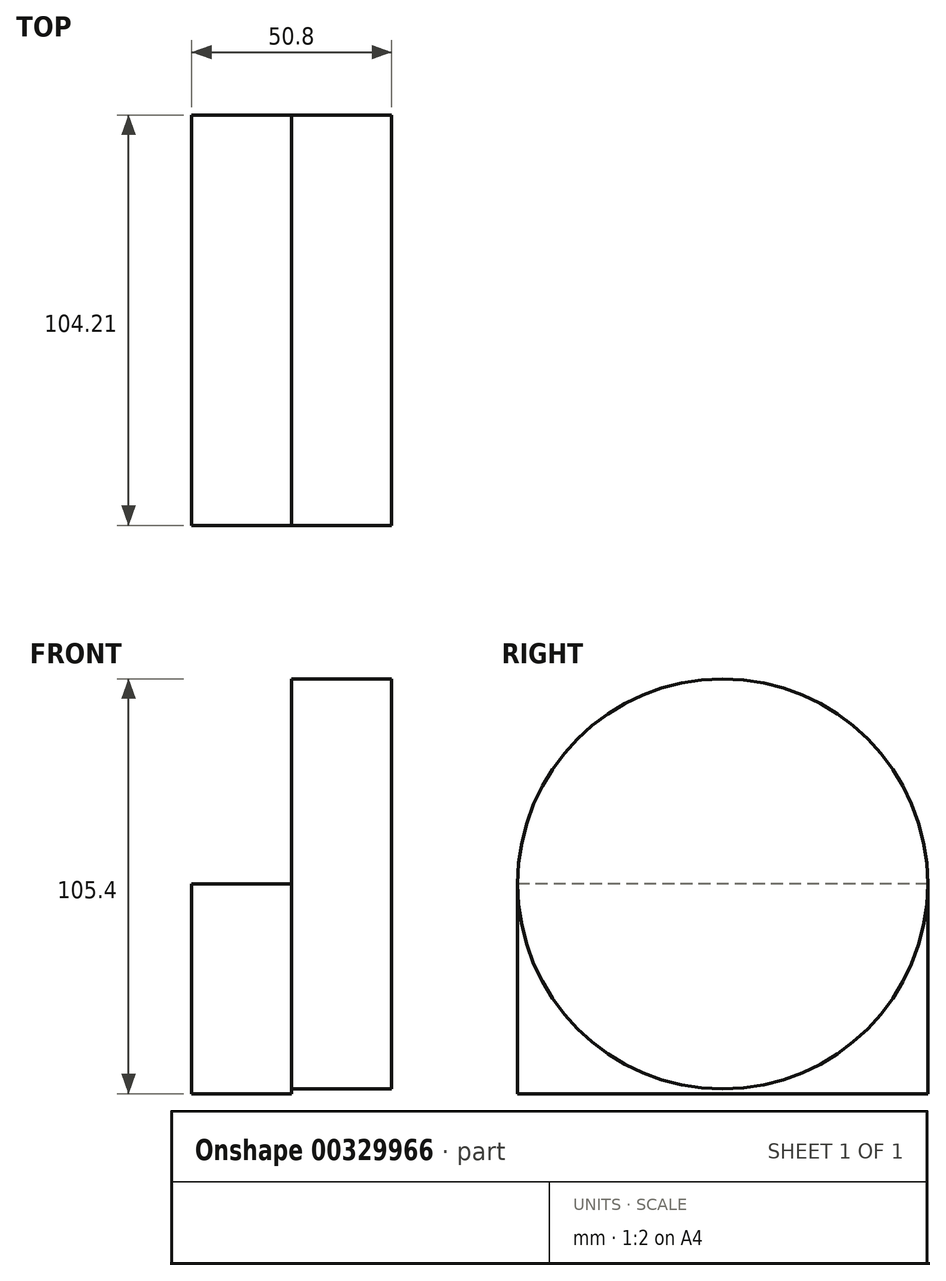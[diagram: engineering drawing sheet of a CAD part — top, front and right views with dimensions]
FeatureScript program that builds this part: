
annotation { "Feature Type Name" : "Feature", "Feature Type Description" : "" }
export const myFeature = defineFeature(function(context is Context, id is Id, definition is map)
    precondition{}
    {
        {
            var Q0;
            Q0=qCreatedBy(makeId("Right.planeOp"),FACE);
            var sketch = newSketch(context, id + "F0", { "sketchPlane" : qUnion([Q0])});
            skLineSegment(sketch, "E0.bottom", {"start": v(52.29, 0) * mm, "end": v(-51.92, 0) * mm});
            skLineSegment(sketch, "E0.top", {"start": v(52.29, 53.3) * mm, "end": v(-51.92, 53.3) * mm});
            skLineSegment(sketch, "E0.left", {"start": v(52.29, 0) * mm, "end": v(52.29, 53.3) * mm});
            skLineSegment(sketch, "E0.right", {"start": v(-51.92, 0) * mm, "end": v(-51.92, 53.3) * mm});
            skSolve(sketch);
        }
        {
            var Q0;
            Q0=makeQuery(id+"F0.imprint","IMPRINT",FACE,{"disambiguationData":[TD([[makeQuery(id+"F0.imprint","IMPRINT",EDGE,{"derivedFrom":sQuery(id+"F0.wireOp",EDGE,"E0.bottom")}),-1.0]])]});
            extrude(context, id + "F1", {"entities" : qUnion([Q0]), "depth" : 25.4 * mm});
        }
        {
            var Q0;
            Q0=makeQuery(id+"F1.opExtrude","CAP_FACE",FACE,{"disambiguationData":[OSD([sQuery(id+"F0.wireOp",EDGE,"E0.bottom"),sQuery(id+"F0.wireOp",EDGE,"E0.top"),sQuery(id+"F0.wireOp",EDGE,"E0.left"),sQuery(id+"F0.wireOp",EDGE,"E0.right")])],"isStart":false});
            var sketch = newSketch(context, id + "F2", { "sketchPlane" : qUnion([Q0])});
            skCircle(sketch, "E1", {"center": v(0.19, 53.3) * mm, "radius": 52.1 * mm});
            skSolve(sketch);
        }
        {
            var Q0;
            Q0 = qSketchRegion(id + "F2", true);
            extrude(context, id + "F3", {"entities" : qUnion([Q0]), "operationType" : NewBodyOperationType.ADD, "depth" : 25.4 * mm});
        }
    });
